# Revit family: Alpha Floodlight
name_source: partatom
category: Lighting Fixtures
units: mm (PartAtom-declared; Revit-internal decimal feet)

## family parameters
Cut with Voids When Loaded = No
Host = Face
Light Source = No
OmniClass Number = 23.80.70.14
OmniClass Title = Luminaries for External Lighting
Part Type = Normal
Room Calculation Point = No
Round Connector Dimension = Use Diameter
Shared = No

## types (1)
- Alpha Floodlight
    Apparent Load = 55 VA
    Default Elevation = 48.000"
    Description = Alpha is More Than a Floodlight … it is a revolutionary design that provides more than just architectural lighting
    Glass = White Glass
    Height = 6.250"
    Lamp = LED,s
    Manufacturer = Beacon Products
    Material Finish = Black
    Model = Alpha Floodlight
    Photometric = ALPHA Light : AL-X-60L-136-4K7-5X5-UNV
    Photometric  Note = More IES files download Photometric Web Link
    Power Factor = 1
    URL = https://www.currentlighting.com
    Voltage = 120 V
    Wattage Comments = 55-220W
    Watts = 55 W

## geometry (parser evidence)
native form markers: Blend x5, Sweep x5
no freeform markers — native parametric forms only
